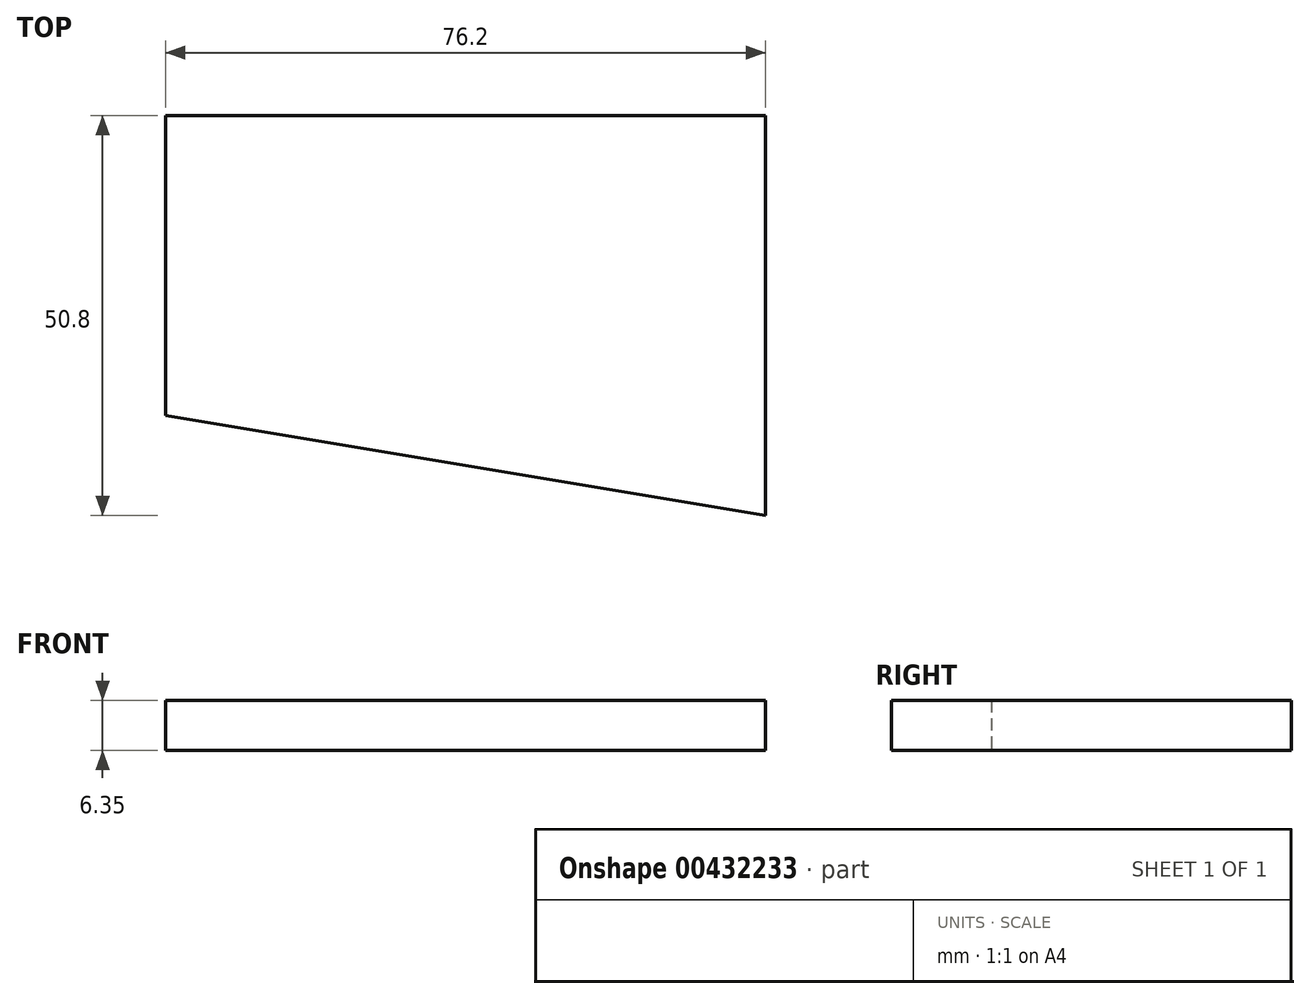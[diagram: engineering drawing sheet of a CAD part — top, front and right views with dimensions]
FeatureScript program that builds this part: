
annotation { "Feature Type Name" : "Feature", "Feature Type Description" : "" }
export const myFeature = defineFeature(function(context is Context, id is Id, definition is map)
    precondition{}
    {
        {
            var Q0;
            Q0=qCreatedBy(makeId("Top.planeOp"),FACE);
            var sketch = newSketch(context, id + "F0", { "sketchPlane" : qUnion([Q0])});
            skLineSegment(sketch, "E0", {"start": v(0, 0) * mm, "end": v(0, 50.8) * mm});
            skLineSegment(sketch, "E1", {"start": v(0, 50.8) * mm, "end": v(-76.2, 50.8) * mm});
            skLineSegment(sketch, "E2", {"start": v(-76.2, 50.8) * mm, "end": v(-76.2, 12.7) * mm});
            skLineSegment(sketch, "E3", {"start": v(-76.2, 12.7) * mm, "end": v(0, 0) * mm});
            skSolve(sketch);
        }
        {
            var Q0;
            Q0 = qSketchRegion(id + "F0", true);
            extrude(context, id + "F1", {"entities" : qUnion([Q0]), "depth" : 6.35 * mm});
        }
    });
